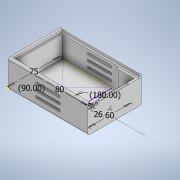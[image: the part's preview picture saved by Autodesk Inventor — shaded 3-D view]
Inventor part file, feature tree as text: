
AUTODESK INVENTOR PART (.ipt)
format: ipt  version: 2020.2 (Build 242310000, 310)  size: 376,320 bytes
history: native  units: mm
features: sketch x12, extrude x11, fillet x2, shell x1
ambient origin geometry x8: Origin, YZ Plane, XZ Plane, XY Plane, X Axis, Y Axis, Z Axis, Center Point
bodies: Solid1 (feature_tree)
feature tree (26):
  extrude  "Extrusion1"  Depth=76.0mm
  shell  "Shell1"  Thickness=40.0mm
  extrude  "Extrusion2"  Depth=3.0mm
  extrude  "Extrusion3"  Depth=3.0mm
  sketch  "Sketch9"  dims[d15=110.5mm d16=0.0mm d17=10.0mm d18=0.0mm]
  extrude  "Extrusion4"  Depth=6.0mm
  extrude  "Extrusion5"  Depth=6.0mm
  fillet  "Fillet1"  [1 undecoded]
  extrude  "Extrusion6"  Depth=3.0mm
  extrude  "Extrusion8"  Depth=10.0mm TaperAngle=0.0deg
  extrude  "Extrusion9"  Depth=2.5mm
  extrude  "Extrusion10"  Depth=5.0mm
  extrude  "Extrusion11"  Depth=5.0mm
  extrude  "Extrusion12"  Depth=2.0mm
  fillet  "Fillet2"  Radius=2.0mm
  sketch  "Sketch1"  dims[d0=112.0mm d1=76.0mm d2=40.0mm d3=0.0mm]
  sketch  "Sketch2"  dims[d4=3.0mm d5=3.0mm]
  sketch  "Sketch3"  dims[d6=0.0mm d7=3.0mm]
  sketch  "Sketch4"  dims[d8=180.0deg d9=6.0mm]
  sketch  "Sketch6"  dims[d10=90.0deg d11=6.0mm d12=90.0deg]
  sketch  "Sketch7"  dims[d13=1.5mm d14=3.0mm]
  sketch  "Sketch10"  dims[d19=20.0mm d20=2.5mm]
  sketch  "Sketch11"  dims[d21=2.0mm d22=-7.853982mm d27=5.0mm]
  sketch  "Sketch12"  dims[d28=0.0mm d29=5.0mm]
  sketch  "Sketch13"  dims[d30=180.0deg d31=2.0mm d32=2.0mm]
  sketch  "Sketch14"  dims[d33=90.0deg d34=3.0mm d35=3.0mm d36=10.0mm d37=0.0mm d38=3.0mm d39=17.0mm d40=8.5mm d41=90.0deg d42=16.0mm d43=0.0mm d44=3.0mm d45=16.0mm d46=0.0mm d47=3.0mm d48=16.0mm d49=0.0mm d50=3.0mm d51=0.0mm d52=0.0mm d55=26.0mm d56=60.0mm d57=5.0mm d58=80.0mm d59=180.0deg d60=75.0mm d61=90.0deg d62=13.0mm d63=15.0mm d64=15.0mm d65=90.0deg d66=10.0mm d67=180.0deg d68=2.0mm d69=10.0mm d70=180.0deg d71=2.0mm d72=4.5mm d73=0.0mm d74=6.25mm d75=5.0mm d76=2.0mm d77=3.0mm d78=-7.853982mm d79=4.0mm d80=4.0mm d81=180.0deg d82=5.0mm d83=5.0mm d84=6.0mm d85=0.0mm d86=4.5mm d87=4.5mm d88=2.0mm d89=-7.853982mm d90=26.0mm d91=26.0mm d92=3.5mm d93=10.0mm d94=0.0mm d95=3.0mm]
note: 1 required parameter value undecoded (feature->parameter linkage not recoverable at this tier; creation-order binding heuristic only, values carry confidence <= 0.55)
